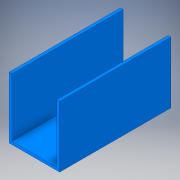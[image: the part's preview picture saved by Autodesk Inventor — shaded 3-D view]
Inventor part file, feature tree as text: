
AUTODESK INVENTOR PART (.ipt)
format: ipt  version: 2019 (Build 230136000, 136)  size: 125,440 bytes
history: native  units: mm
features: extrude x2, sketch x2, projected_geometry x1
ambient origin geometry x8: Origin, YZ Plane, XZ Plane, XY Plane, X Axis, Y Axis, Z Axis, Center Point
bodies: Solid1 (feature_tree)
feature tree (5):
  extrude  "Extrusion1"  Depth=124.08mm
  extrude  "Extrusion3"  Depth=68.18mm
  sketch  "Sketch1"  dims[d0=50.0mm d1=124.08mm]
  sketch  "Sketch4"  dims[d2=10.0mm d3=44.45mm d4=25.0mm d5=3.18mm d6=0.0mm d11=3.18mm d12=3.18mm d13=68.18mm d14=0.0mm]
  projected_geometry  "Projected Loop2"
